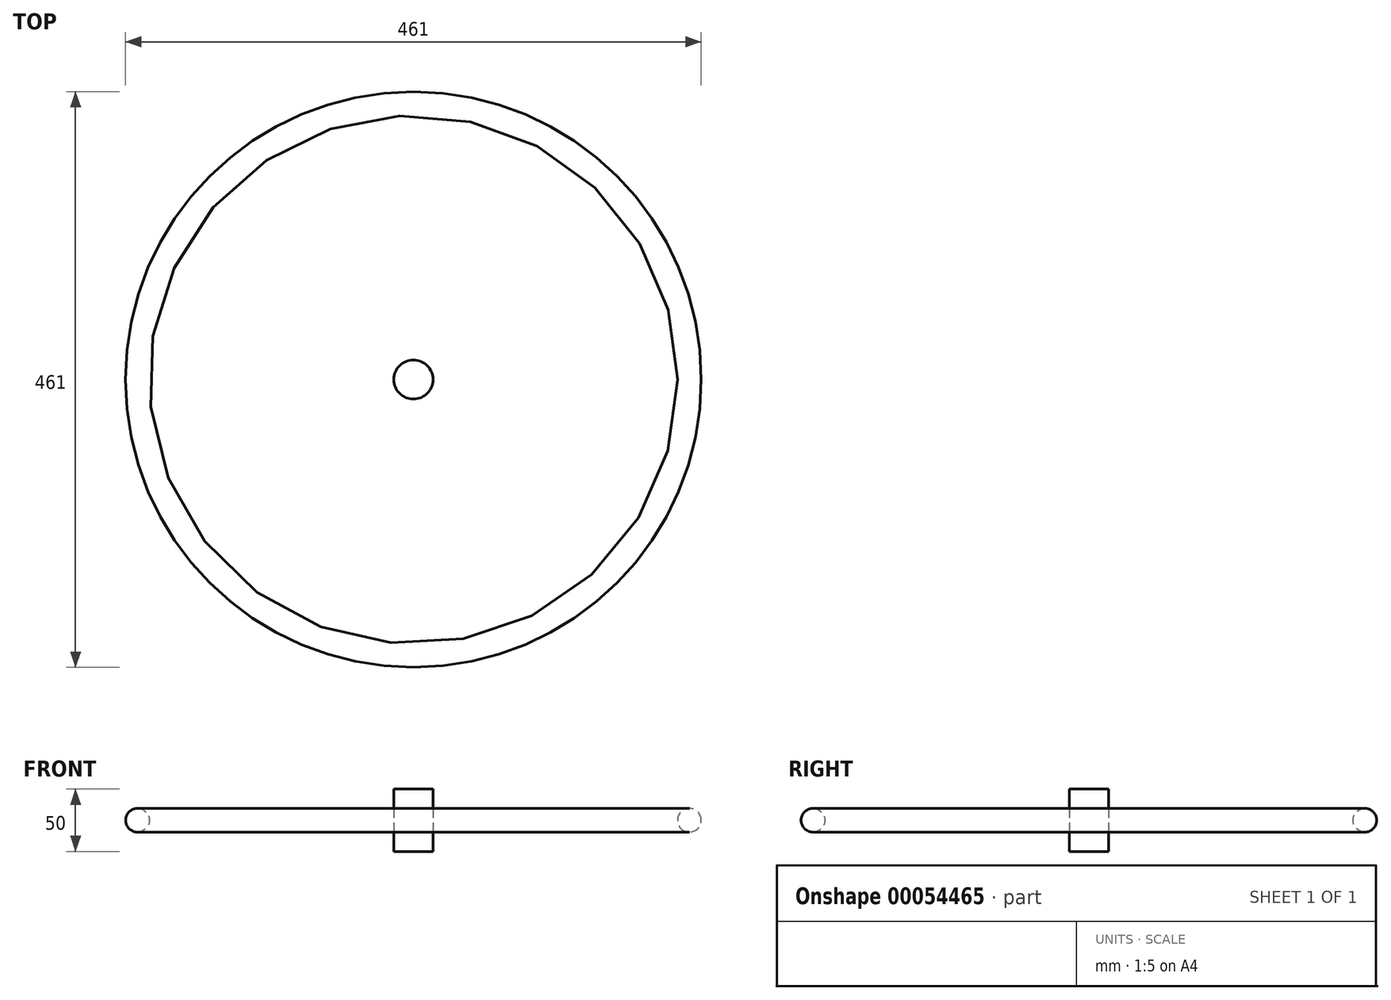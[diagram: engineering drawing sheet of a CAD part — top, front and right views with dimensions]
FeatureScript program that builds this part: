
annotation { "Feature Type Name" : "Feature", "Feature Type Description" : "" }
export const myFeature = defineFeature(function(context is Context, id is Id, definition is map)
    precondition{}
    {
        {
            var Q0;
            Q0=qCreatedBy(makeId("Right.planeOp"),FACE);
            var sketch = newSketch(context, id + "F0", { "sketchPlane" : qUnion([Q0])});
            skCircle(sketch, "E0", {"center": v(-221, 0) * mm, "radius": 9.5 * mm});
            skLineSegment(sketch, "E1", {"start": v(0, 57.96) * mm, "end": v(0, -58.22) * mm, "construction": true});
            skSolve(sketch);
        }
        {
            var Q0;
            Q0=makeQuery(id+"F0.imprint","IMPRINT",FACE,{"disambiguationData":[TD([[makeQuery(id+"F0.imprint","IMPRINT",EDGE,{"derivedFrom":sQuery(id+"F0.wireOp",EDGE,"E0")}),1.0]])]});
            var Q1;
            Q1=sQuery(id+"F0.wireOp",EDGE,"E1");
            revolve(context, id + "F1", {"entities" : qUnion([Q0]), "axis" : qUnion([Q1]), "revolveType" : RevolveType.FULL});
        }
        {
            var Q0;
            Q0=qCreatedBy(makeId("Top.planeOp"),FACE);
            var sketch = newSketch(context, id + "F2", { "sketchPlane" : qUnion([Q0])});
            skCircle(sketch, "E2", {"center": v(0, 0) * mm, "radius": 15.68 * mm});
            skSolve(sketch);
        }
        {
            var Q0;
            Q0=makeQuery(id+"F2.imprint","IMPRINT",FACE,{"disambiguationData":[TD([[makeQuery(id+"F2.imprint","IMPRINT",EDGE,{"derivedFrom":sQuery(id+"F2.wireOp",EDGE,"E2")}),1.0]])]});
            extrude(context, id + "F3", {"entities" : qUnion([Q0]), "depth" : 25 * mm, "hasSecondDirection" : true, "secondDirectionOppositeDirection" : true, "secondDirectionDepth" : 25 * mm});
        }
    });
